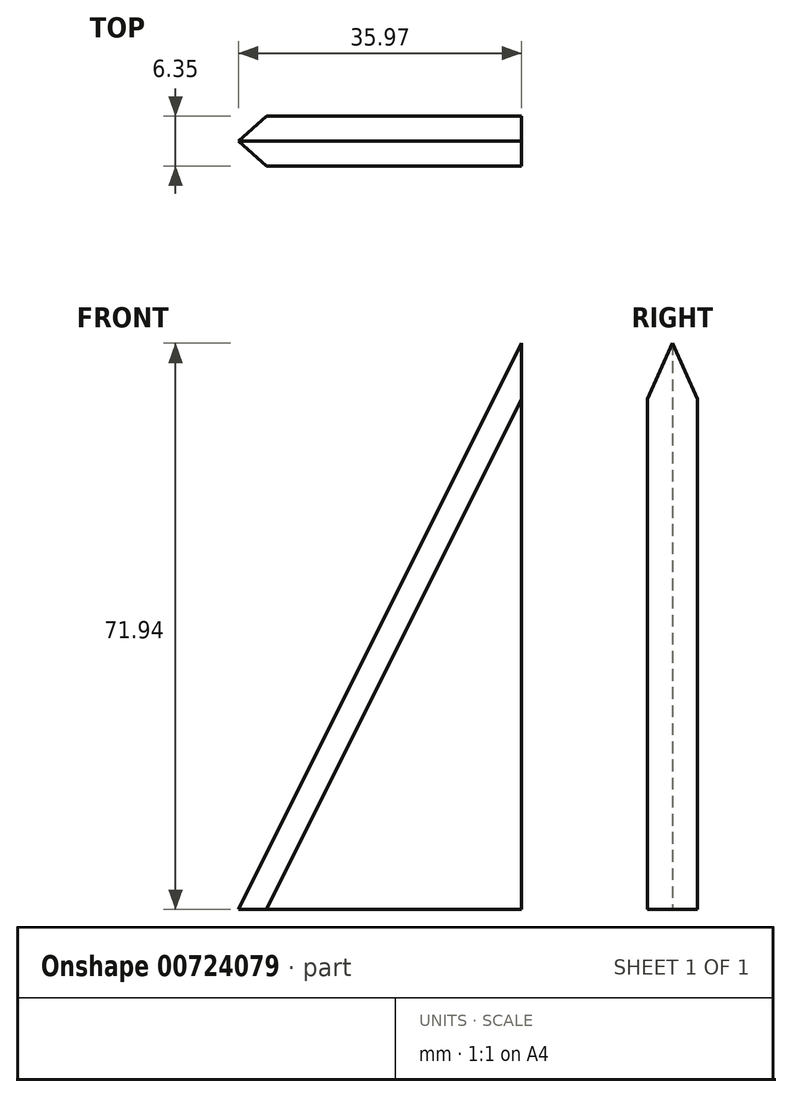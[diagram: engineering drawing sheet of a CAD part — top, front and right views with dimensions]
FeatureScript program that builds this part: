
annotation { "Feature Type Name" : "Feature", "Feature Type Description" : "" }
export const myFeature = defineFeature(function(context is Context, id is Id, definition is map)
    precondition{}
    {
        {
            var Q0;
            Q0=qCreatedBy(makeId("Front.planeOp"),FACE);
            var sketch = newSketch(context, id + "F0", { "sketchPlane" : qUnion([Q0])});
            skLineSegment(sketch, "E0", {"start": v(0, 0) * mm, "end": v(38.1, 0) * mm});
            skLineSegment(sketch, "E1", {"start": v(38.1, 0) * mm, "end": v(38.1, 76.2) * mm});
            skLineSegment(sketch, "E2", {"start": v(38.1, 76.2) * mm, "end": v(0, 0) * mm});
            skSolve(sketch);
        }
        {
            var Q0;
            Q0=makeQuery(id+"F0.imprint","IMPRINT",FACE,{"disambiguationData":[TD([[makeQuery(id+"F0.imprint","IMPRINT",EDGE,{"derivedFrom":sQuery(id+"F0.wireOp",EDGE,"E0")}),1.0]])]});
            extrude(context, id + "F1", {"entities" : qUnion([Q0]), "depth" : 6.35 * mm, "offsetDistance" : 25.4 * mm});
        }
        {
            var Q0;
            Q0=makeQuery(id+"F1.opExtrude","CAP_EDGE",EDGE,{"disambiguationData":[OSD([sQuery(id+"F0.wireOp",EDGE,"E2")])],"isStart":false});
            var Q1;
            Q1=makeQuery(id+"F1.opExtrude","CAP_EDGE",EDGE,{"disambiguationData":[OSD([sQuery(id+"F0.wireOp",EDGE,"E2")])],"isStart":true});
            chamfer(context, id + "F2", {"entities" : qUnion([Q0, Q1]), "width" : 5.08 * mm, "tangentPropagation" : true});
        }
    });
